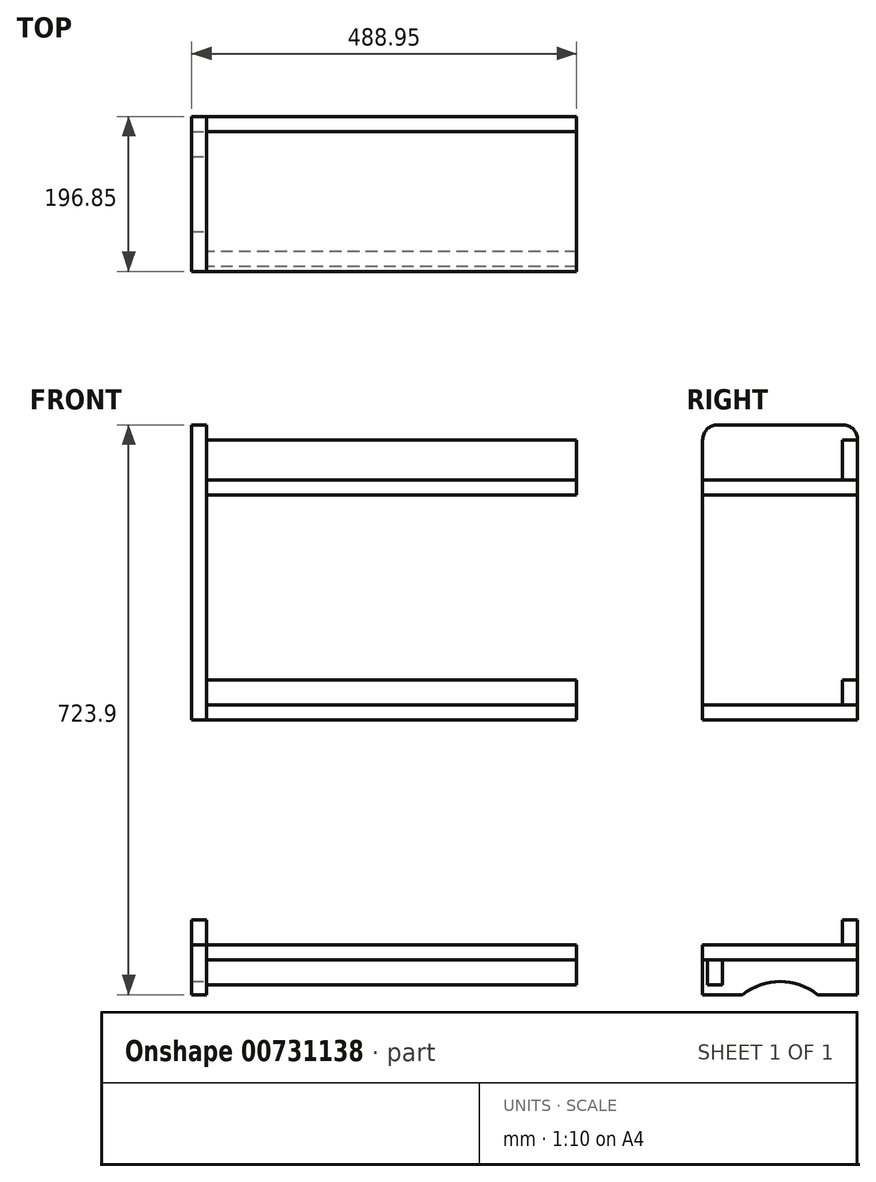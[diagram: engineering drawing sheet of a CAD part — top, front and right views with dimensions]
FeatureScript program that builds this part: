
annotation { "Feature Type Name" : "Feature", "Feature Type Description" : "" }
export const myFeature = defineFeature(function(context is Context, id is Id, definition is map)
    precondition{}
    {
        {
            var Q0;
            Q0=qCreatedBy(makeId("Right.planeOp"),FACE);
            var sketch = newSketch(context, id + "F0", { "sketchPlane" : qUnion([Q0])});
            skLineSegment(sketch, "E0", {"start": v(95.25, -50.98) * mm, "end": v(146.05, -50.98) * mm});
            skLineSegment(sketch, "E1", {"start": v(146.05, -50.98) * mm, "end": v(146.05, 672.92) * mm});
            skLineSegment(sketch, "E2", {"start": v(146.05, 672.92) * mm, "end": v(-50.8, 672.92) * mm});
            skLineSegment(sketch, "E3", {"start": v(-50.8, 672.92) * mm, "end": v(-50.8, -50.98) * mm});
            skLineSegment(sketch, "E4", {"start": v(-50.8, -50.98) * mm, "end": v(0, -50.98) * mm});
            skArc(sketch, "E5", {"start": v(95.25, -50.98) * mm, "mid": v(47.63, -34.27) * mm, "end": v(0, -50.98) * mm});
            skLineSegment(sketch, "E6.bottom", {"start": v(146.05, 653.87) * mm, "end": v(127, 653.87) * mm});
            skLineSegment(sketch, "E6.top", {"start": v(146.05, 603.07) * mm, "end": v(127, 603.07) * mm});
            skLineSegment(sketch, "E6.left", {"start": v(146.05, 653.87) * mm, "end": v(146.05, 603.07) * mm});
            skLineSegment(sketch, "E6.right", {"start": v(127, 653.87) * mm, "end": v(127, 603.07) * mm});
            skLineSegment(sketch, "E7.bottom", {"start": v(-25.4, -38.28) * mm, "end": v(-44.45, -38.28) * mm});
            skLineSegment(sketch, "E7.top", {"start": v(-25.4, -6.53) * mm, "end": v(-44.45, -6.53) * mm});
            skLineSegment(sketch, "E7.left", {"start": v(-25.4, -38.28) * mm, "end": v(-25.4, -6.53) * mm});
            skLineSegment(sketch, "E7.right", {"start": v(-44.45, -38.28) * mm, "end": v(-44.45, -6.53) * mm});
            skLineSegment(sketch, "E8.bottom", {"start": v(146.05, -6.53) * mm, "end": v(-50.8, -6.53) * mm});
            skLineSegment(sketch, "E8.top", {"start": v(146.05, 12.52) * mm, "end": v(-50.8, 12.52) * mm});
            skLineSegment(sketch, "E8.left", {"start": v(146.05, -6.53) * mm, "end": v(146.05, 12.52) * mm});
            skLineSegment(sketch, "E8.right", {"start": v(-50.8, -6.53) * mm, "end": v(-50.8, 12.52) * mm});
            skPoint(sketch, "E9.firstSnap0", {"position": v(47.63, 672.92) * mm});
            skLineSegment(sketch, "E10.bottom", {"start": v(146.05, 603.07) * mm, "end": v(-50.8, 603.07) * mm});
            skLineSegment(sketch, "E10.top", {"start": v(146.05, 584.02) * mm, "end": v(-50.8, 584.02) * mm});
            skLineSegment(sketch, "E10.left", {"start": v(146.05, 603.07) * mm, "end": v(146.05, 584.02) * mm});
            skLineSegment(sketch, "E10.right", {"start": v(-50.8, 603.07) * mm, "end": v(-50.8, 584.02) * mm});
            skLineSegment(sketch, "E11.bottom", {"start": v(146.05, 349.07) * mm, "end": v(127, 349.07) * mm});
            skLineSegment(sketch, "E11.top", {"start": v(146.05, 317.32) * mm, "end": v(127, 317.32) * mm});
            skLineSegment(sketch, "E11.left", {"start": v(146.05, 349.07) * mm, "end": v(146.05, 317.32) * mm});
            skLineSegment(sketch, "E11.right", {"start": v(127, 349.07) * mm, "end": v(127, 317.32) * mm});
            skLineSegment(sketch, "E12.bottom", {"start": v(146.05, 317.32) * mm, "end": v(-50.8, 317.32) * mm});
            skLineSegment(sketch, "E12.top", {"start": v(146.05, 298.27) * mm, "end": v(-50.8, 298.27) * mm});
            skLineSegment(sketch, "E12.left", {"start": v(146.05, 317.32) * mm, "end": v(146.05, 298.27) * mm});
            skLineSegment(sketch, "E12.right", {"start": v(-50.8, 317.32) * mm, "end": v(-50.8, 298.27) * mm});
            skLineSegment(sketch, "E13.bottom", {"start": v(146.05, 12.52) * mm, "end": v(127, 12.52) * mm});
            skLineSegment(sketch, "E13.top", {"start": v(146.05, 44.27) * mm, "end": v(127, 44.27) * mm});
            skLineSegment(sketch, "E13.left", {"start": v(146.05, 12.52) * mm, "end": v(146.05, 44.27) * mm});
            skLineSegment(sketch, "E13.right", {"start": v(127, 12.52) * mm, "end": v(127, 44.27) * mm});
            skSolve(sketch);
        }
        {
            var Q0;
            Q0=makeQuery(id+"F0.imprint","IMPRINT",FACE,{"disambiguationData":[TD([[makeQuery(id+"F0.imprint","IMPRINT",EDGE,{"derivedFrom":sQuery(id+"F0.wireOp",EDGE,"E6.bottom")}),1.0]])]});
            var Q1;
            {var subQ2=sQuery(id+"F0.wireOp",EDGE,"E2");Q1=makeQuery(id+"F0.imprint","IMPRINT",FACE,{"disambiguationData":[TD([[makeQuery(id+"F0.imprint","IMPRINT",EDGE,{"derivedFrom":subQ2}),1.0]])]});}
            var Q2;
            Q2=makeQuery(id+"F0.imprint","IMPRINT",FACE,{"disambiguationData":[TD([[makeQuery(id+"F0.imprint","IMPRINT",EDGE,{"derivedFrom":sQuery(id+"F0.wireOp",EDGE,"E10.top")}),-1.0]])]});
            var Q3;
            {var subQ1=sQuery(id+"F0.wireOp",EDGE,"E10.top");Q3=makeQuery(id+"F0.imprint","IMPRINT",FACE,{"disambiguationData":[TD([[makeQuery(id+"F0.imprint","IMPRINT",EDGE,{"derivedFrom":subQ1}),1.0]])]});}
            var Q4;
            Q4=makeQuery(id+"F0.imprint","IMPRINT",FACE,{"disambiguationData":[TD([[makeQuery(id+"F0.imprint","IMPRINT",EDGE,{"derivedFrom":sQuery(id+"F0.wireOp",EDGE,"E11.bottom")}),1.0]])]});
            var Q5;
            Q5=makeQuery(id+"F0.imprint","IMPRINT",FACE,{"disambiguationData":[TD([[makeQuery(id+"F0.imprint","IMPRINT",EDGE,{"derivedFrom":sQuery(id+"F0.wireOp",EDGE,"E12.top")}),-1.0]])]});
            var Q6;
            {var subQ1=sQuery(id+"F0.wireOp",EDGE,"E8.top");Q6=makeQuery(id+"F0.imprint","IMPRINT",FACE,{"disambiguationData":[TD([[makeQuery(id+"F0.imprint","IMPRINT",EDGE,{"derivedFrom":subQ1}),-1.0]])]});}
            var Q7;
            Q7=makeQuery(id+"F0.imprint","IMPRINT",FACE,{"disambiguationData":[TD([[makeQuery(id+"F0.imprint","IMPRINT",EDGE,{"derivedFrom":sQuery(id+"F0.wireOp",EDGE,"E13.bottom")}),-1.0]])]});
            var Q8;
            {var subQ6=sQuery(id+"F0.wireOp",EDGE,"E0");Q8=makeQuery(id+"F0.imprint","IMPRINT",FACE,{"disambiguationData":[TD([[makeQuery(id+"F0.imprint","IMPRINT",EDGE,{"derivedFrom":subQ6}),1.0]])]});}
            var Q9;
            Q9=makeQuery(id+"F0.imprint","IMPRINT",FACE,{"disambiguationData":[TD([[makeQuery(id+"F0.imprint","IMPRINT",EDGE,{"derivedFrom":sQuery(id+"F0.wireOp",EDGE,"E7.bottom")}),-1.0]])]});
            var Q10;
            Q10=makeQuery(id+"F0.imprint","IMPRINT",FACE,{"disambiguationData":[TD([[makeQuery(id+"F0.imprint","IMPRINT",EDGE,{"derivedFrom":sQuery(id+"F0.wireOp",EDGE,"E8.top")}),1.0]])]});
            extrude(context, id + "F1", {"entities" : qUnion([Q0, Q1, Q2, Q3, Q4, Q5, Q6, Q7, Q8, Q9, Q10]), "oppositeDirection" : true, "depth" : 19.05 * mm, "offsetDistance" : 25.4 * mm});
        }
        {
            var Q0;
            Q0=makeQuery(id+"F0.imprint","IMPRINT",FACE,{"disambiguationData":[TD([[makeQuery(id+"F0.imprint","IMPRINT",EDGE,{"derivedFrom":sQuery(id+"F0.wireOp",EDGE,"E6.bottom")}),1.0]])]});
            var Q1;
            Q1=makeQuery(id+"F0.imprint","IMPRINT",FACE,{"disambiguationData":[TD([[makeQuery(id+"F0.imprint","IMPRINT",EDGE,{"derivedFrom":sQuery(id+"F0.wireOp",EDGE,"E11.bottom")}),1.0]])]});
            var Q2;
            Q2=makeQuery(id+"F0.imprint","IMPRINT",FACE,{"disambiguationData":[TD([[makeQuery(id+"F0.imprint","IMPRINT",EDGE,{"derivedFrom":sQuery(id+"F0.wireOp",EDGE,"E13.bottom")}),-1.0]])]});
            var Q3;
            Q3=makeQuery(id+"F0.imprint","IMPRINT",FACE,{"disambiguationData":[TD([[makeQuery(id+"F0.imprint","IMPRINT",EDGE,{"derivedFrom":sQuery(id+"F0.wireOp",EDGE,"E7.bottom")}),-1.0]])]});
            extrude(context, id + "F2", {"entities" : qUnion([Q0, Q1, Q2, Q3]), "depth" : 469.9 * mm, "offsetDistance" : 25.4 * mm});
        }
        {
            var Q0;
            Q0=makeQuery(id+"F0.imprint","IMPRINT",FACE,{"disambiguationData":[TD([[makeQuery(id+"F0.imprint","IMPRINT",EDGE,{"derivedFrom":sQuery(id+"F0.wireOp",EDGE,"E10.top")}),-1.0]])]});
            var Q1;
            Q1=makeQuery(id+"F0.imprint","IMPRINT",FACE,{"disambiguationData":[TD([[makeQuery(id+"F0.imprint","IMPRINT",EDGE,{"derivedFrom":sQuery(id+"F0.wireOp",EDGE,"E12.top")}),-1.0]])]});
            var Q2;
            Q2=makeQuery(id+"F0.imprint","IMPRINT",FACE,{"disambiguationData":[TD([[makeQuery(id+"F0.imprint","IMPRINT",EDGE,{"derivedFrom":sQuery(id+"F0.wireOp",EDGE,"E8.top")}),1.0]])]});
            extrude(context, id + "F3", {"entities" : qUnion([Q0, Q1, Q2]), "depth" : 469.9 * mm, "offsetDistance" : 25.4 * mm});
        }
        {
            var Q0;
            Q0=makeQuery(id+"F1.opExtrude","SWEPT_EDGE",EDGE,{"disambiguationData":[OSD([sQuery(id+"F0.wireOp",EDGE,"E1"),sQuery(id+"F0.wireOp",EDGE,"E2")])]});
            var Q1;
            Q1=makeQuery(id+"F1.opExtrude","SWEPT_EDGE",EDGE,{"disambiguationData":[OSD([sQuery(id+"F0.wireOp",EDGE,"E2"),sQuery(id+"F0.wireOp",EDGE,"E3")])]});
            fillet(context, id + "F4", {"entities" : qUnion([Q0, Q1]), "radius" : 19.05 * mm, "tangentPropagation" : true, "allowEdgeOverflow" : false});
        }
    });
